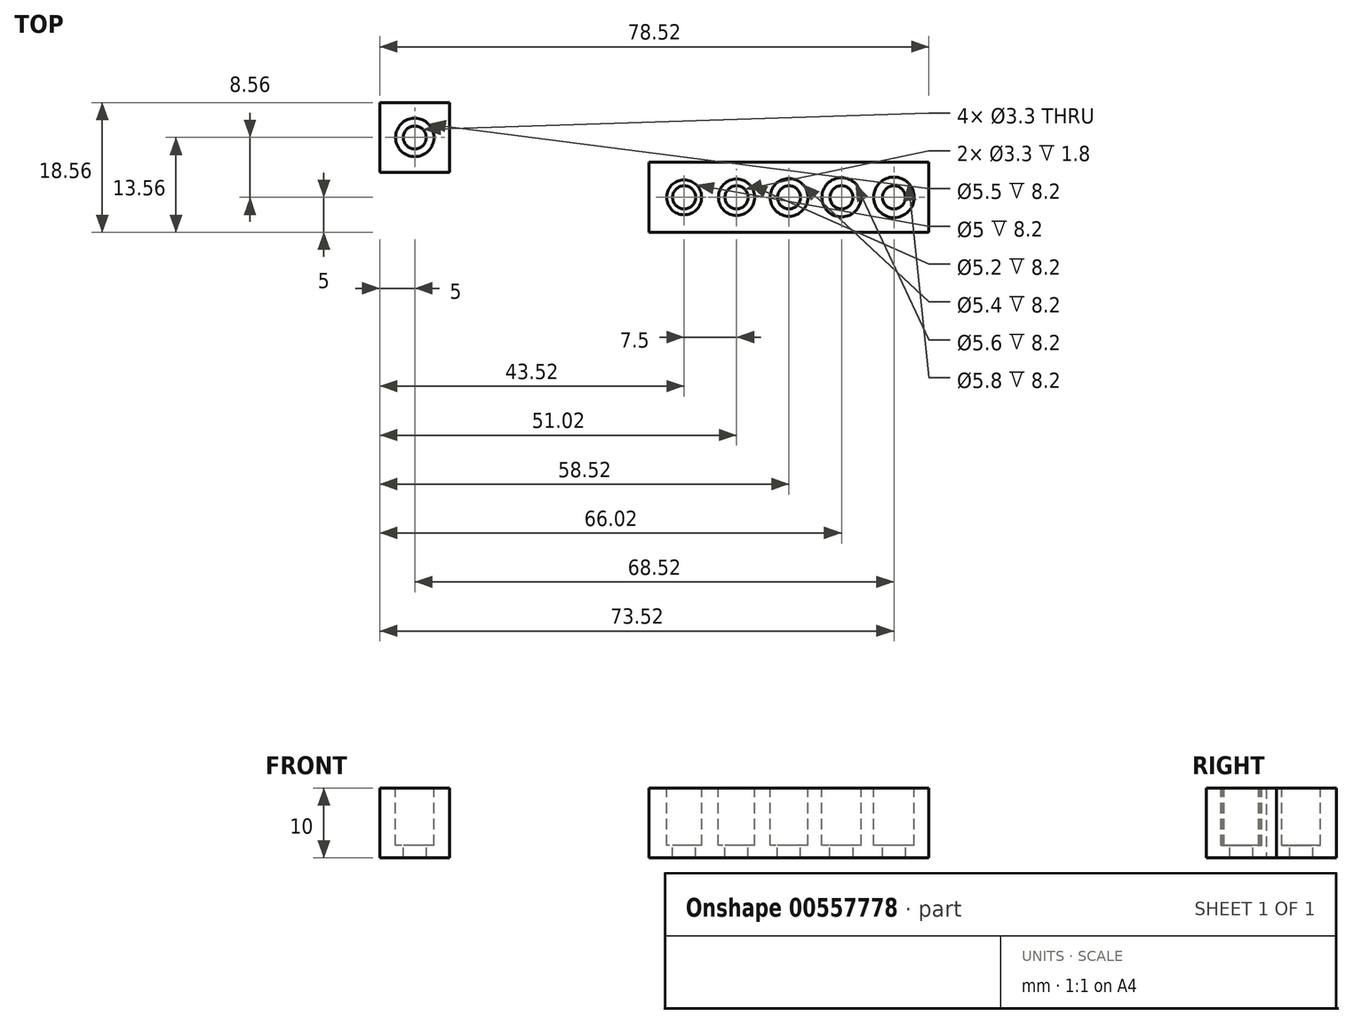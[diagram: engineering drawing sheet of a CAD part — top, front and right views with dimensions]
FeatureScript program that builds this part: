
annotation { "Feature Type Name" : "Feature", "Feature Type Description" : "" }
export const myFeature = defineFeature(function(context is Context, id is Id, definition is map)
    precondition{}
    {
        {
            var Q0;
            Q0=qCreatedBy(makeId("Top.planeOp"),FACE);
            var sketch = newSketch(context, id + "F0", { "sketchPlane" : qUnion([Q0])});
            skLineSegment(sketch, "E0.bottom", {"start": v(0, 0) * mm, "end": v(40, 0) * mm});
            skLineSegment(sketch, "E0.top", {"start": v(0, 10) * mm, "end": v(40, 10) * mm});
            skLineSegment(sketch, "E0.left", {"start": v(0, 0) * mm, "end": v(0, 10) * mm});
            skLineSegment(sketch, "E0.right", {"start": v(40, 0) * mm, "end": v(40, 10) * mm});
            skLineSegment(sketch, "E1", {"start": v(0, 5) * mm, "end": v(40, 5) * mm, "construction": true});
            skSolve(sketch);
        }
        {
            var Q0;
            Q0=makeQuery(id+"F0.imprint","IMPRINT",FACE,{"disambiguationData":[TD([[makeQuery(id+"F0.imprint","IMPRINT",EDGE,{"derivedFrom":sQuery(id+"F0.wireOp",EDGE,"E0.bottom")}),1.0]])]});
            extrude(context, id + "F1", {"entities" : qUnion([Q0]), "depth" : 10 * mm, "offsetDistance" : 25 * mm});
        }
        {
            var Q0;
            Q0=makeQuery(id+"F1.opExtrude","CAP_FACE",FACE,{"disambiguationData":[OSD([sQuery(id+"F0.wireOp",EDGE,"E0.bottom"),sQuery(id+"F0.wireOp",EDGE,"E0.top"),sQuery(id+"F0.wireOp",EDGE,"E0.left"),sQuery(id+"F0.wireOp",EDGE,"E0.right")])],"isStart":false});
            var sketch = newSketch(context, id + "F2", { "sketchPlane" : qUnion([Q0])});
            skLineSegment(sketch, "E2", {"start": v(0, 5) * mm, "end": v(40, 5) * mm, "construction": true});
            skPoint(sketch, "E3", {"position": v(5, 5) * mm});
            skPoint(sketch, "E4.1.0.0", {"position": v(12.5, 5) * mm});
            skPoint(sketch, "E4.2.0.0", {"position": v(20, 5) * mm});
            skPoint(sketch, "E4.3.0.0", {"position": v(27.5, 5) * mm});
            skPoint(sketch, "E4.4.0.0", {"position": v(35, 5) * mm});
            skLineSegment(sketch, "E4.direction1", {"start": v(5, 5) * mm, "end": v(12.5, 5) * mm, "construction": true});
            skSolve(sketch);
        }
        {
            var Q0;
            Q0=sQuery(id+"F2.wireOp",VERTEX,"E3");
            var Q1;
            Q1=makeQuery(id+"F1.opExtrude","SWEPT_BODY",BODY,{"disambiguationData":[OSD([sQuery(id+"F0.wireOp",EDGE,"E0.bottom"),sQuery(id+"F0.wireOp",EDGE,"E0.top"),sQuery(id+"F0.wireOp",EDGE,"E0.left"),sQuery(id+"F0.wireOp",EDGE,"E0.right")])]});
            hole(context, id + "F3", {"style" : HoleStyle.C_BORE, "endStyle" : HoleEndStyle.THROUGH, "holeDiameter" : 3.3 * mm, "cBoreDiameter" : 5 * mm, "cBoreDepth" : 8.2 * mm, "majorDiameter" : 5 * mm, "isTappedThrough" : true, "tappedDepth" : 12 * mm, "tapClearance" : 3, "locations" : qUnion([Q0]), "scope" : qUnion([Q1])});
        }
        {
            var Q0;
            Q0=sQuery(id+"F2.wireOp",VERTEX,"E4.1.0.0");
            var Q1;
            Q1=makeQuery(id+"F1.opExtrude","SWEPT_BODY",BODY,{"disambiguationData":[OSD([sQuery(id+"F0.wireOp",EDGE,"E0.bottom"),sQuery(id+"F0.wireOp",EDGE,"E0.top"),sQuery(id+"F0.wireOp",EDGE,"E0.left"),sQuery(id+"F0.wireOp",EDGE,"E0.right")])]});
            hole(context, id + "F4", {"style" : HoleStyle.C_BORE, "endStyle" : HoleEndStyle.THROUGH, "holeDiameter" : 3.3 * mm, "cBoreDiameter" : 5.2 * mm, "cBoreDepth" : 8.2 * mm, "majorDiameter" : 5 * mm, "isTappedThrough" : true, "tappedDepth" : 12 * mm, "tapClearance" : 3, "locations" : qUnion([Q0]), "scope" : qUnion([Q1])});
        }
        {
            var Q0;
            Q0=sQuery(id+"F2.wireOp",VERTEX,"E4.2.0.0");
            var Q1;
            Q1=makeQuery(id+"F1.opExtrude","SWEPT_BODY",BODY,{"disambiguationData":[OSD([sQuery(id+"F0.wireOp",EDGE,"E0.bottom"),sQuery(id+"F0.wireOp",EDGE,"E0.top"),sQuery(id+"F0.wireOp",EDGE,"E0.left"),sQuery(id+"F0.wireOp",EDGE,"E0.right")])]});
            hole(context, id + "F5", {"style" : HoleStyle.C_BORE, "endStyle" : HoleEndStyle.THROUGH, "holeDiameter" : 3.3 * mm, "cBoreDiameter" : 5.4 * mm, "cBoreDepth" : 8.2 * mm, "majorDiameter" : 5 * mm, "isTappedThrough" : true, "tappedDepth" : 12 * mm, "tapClearance" : 3, "locations" : qUnion([Q0]), "scope" : qUnion([Q1])});
        }
        {
            var Q0;
            Q0=sQuery(id+"F2.wireOp",VERTEX,"E4.3.0.0");
            var Q1;
            Q1=makeQuery(id+"F1.opExtrude","SWEPT_BODY",BODY,{"disambiguationData":[OSD([sQuery(id+"F0.wireOp",EDGE,"E0.bottom"),sQuery(id+"F0.wireOp",EDGE,"E0.top"),sQuery(id+"F0.wireOp",EDGE,"E0.left"),sQuery(id+"F0.wireOp",EDGE,"E0.right")])]});
            hole(context, id + "F6", {"style" : HoleStyle.C_BORE, "endStyle" : HoleEndStyle.THROUGH, "holeDiameter" : 3.3 * mm, "cBoreDiameter" : 5.6 * mm, "cBoreDepth" : 8.2 * mm, "majorDiameter" : 5 * mm, "isTappedThrough" : true, "tappedDepth" : 12 * mm, "tapClearance" : 3, "locations" : qUnion([Q0]), "scope" : qUnion([Q1])});
        }
        {
            var Q0;
            Q0=sQuery(id+"F2.wireOp",VERTEX,"E4.4.0.0");
            var Q1;
            Q1=makeQuery(id+"F1.opExtrude","SWEPT_BODY",BODY,{"disambiguationData":[OSD([sQuery(id+"F0.wireOp",EDGE,"E0.bottom"),sQuery(id+"F0.wireOp",EDGE,"E0.top"),sQuery(id+"F0.wireOp",EDGE,"E0.left"),sQuery(id+"F0.wireOp",EDGE,"E0.right")])]});
            hole(context, id + "F7", {"style" : HoleStyle.C_BORE, "endStyle" : HoleEndStyle.THROUGH, "holeDiameter" : 3.3 * mm, "cBoreDiameter" : 5.8 * mm, "cBoreDepth" : 8.2 * mm, "majorDiameter" : 5 * mm, "isTappedThrough" : true, "tappedDepth" : 12 * mm, "tapClearance" : 3, "locations" : qUnion([Q0]), "scope" : qUnion([Q1])});
        }
        {
            var Q0;
            Q0=qCreatedBy(makeId("Top.planeOp"),FACE);
            var sketch = newSketch(context, id + "F8", { "sketchPlane" : qUnion([Q0])});
            skLineSegment(sketch, "E5.bottom", {"start": v(-38.52, 8.56) * mm, "end": v(-28.52, 8.56) * mm});
            skLineSegment(sketch, "E5.top", {"start": v(-38.52, 18.56) * mm, "end": v(-28.52, 18.56) * mm});
            skLineSegment(sketch, "E5.left", {"start": v(-38.52, 8.56) * mm, "end": v(-38.52, 18.56) * mm});
            skLineSegment(sketch, "E5.right", {"start": v(-28.52, 8.56) * mm, "end": v(-28.52, 18.56) * mm});
            skSolve(sketch);
        }
        {
            var Q0;
            Q0=makeQuery(id+"F8.imprint","IMPRINT",FACE,{"disambiguationData":[TD([[makeQuery(id+"F8.imprint","IMPRINT",EDGE,{"derivedFrom":sQuery(id+"F8.wireOp",EDGE,"E5.bottom")}),1.0]])]});
            extrude(context, id + "F9", {"entities" : qUnion([Q0]), "depth" : 10 * mm, "offsetDistance" : 25 * mm});
        }
        {
            var Q0;
            Q0=makeQuery(id+"F9.opExtrude","CAP_FACE",FACE,{"disambiguationData":[OSD([sQuery(id+"F8.wireOp",EDGE,"E5.bottom"),sQuery(id+"F8.wireOp",EDGE,"E5.top"),sQuery(id+"F8.wireOp",EDGE,"E5.left"),sQuery(id+"F8.wireOp",EDGE,"E5.right")])],"isStart":false});
            var sketch = newSketch(context, id + "F10", { "sketchPlane" : qUnion([Q0])});
            skPoint(sketch, "E6", {"position": v(-33.52, 13.56) * mm});
            skSolve(sketch);
        }
        {
            var Q0;
            Q0=sQuery(id+"F10.wireOp",VERTEX,"E6");
            var Q1;
            Q1=makeQuery(id+"F9.opExtrude","SWEPT_BODY",BODY,{"disambiguationData":[OSD([sQuery(id+"F8.wireOp",EDGE,"E5.bottom"),sQuery(id+"F8.wireOp",EDGE,"E5.top"),sQuery(id+"F8.wireOp",EDGE,"E5.left"),sQuery(id+"F8.wireOp",EDGE,"E5.right")])]});
            hole(context, id + "F11", {"style" : HoleStyle.C_BORE, "endStyle" : HoleEndStyle.THROUGH, "holeDiameter" : 3.3 * mm, "cBoreDiameter" : 5.5 * mm, "cBoreDepth" : 8.2 * mm, "majorDiameter" : 5 * mm, "isTappedThrough" : true, "tappedDepth" : 12 * mm, "tapClearance" : 3, "locations" : qUnion([Q0]), "scope" : qUnion([Q1])});
        }
    });
